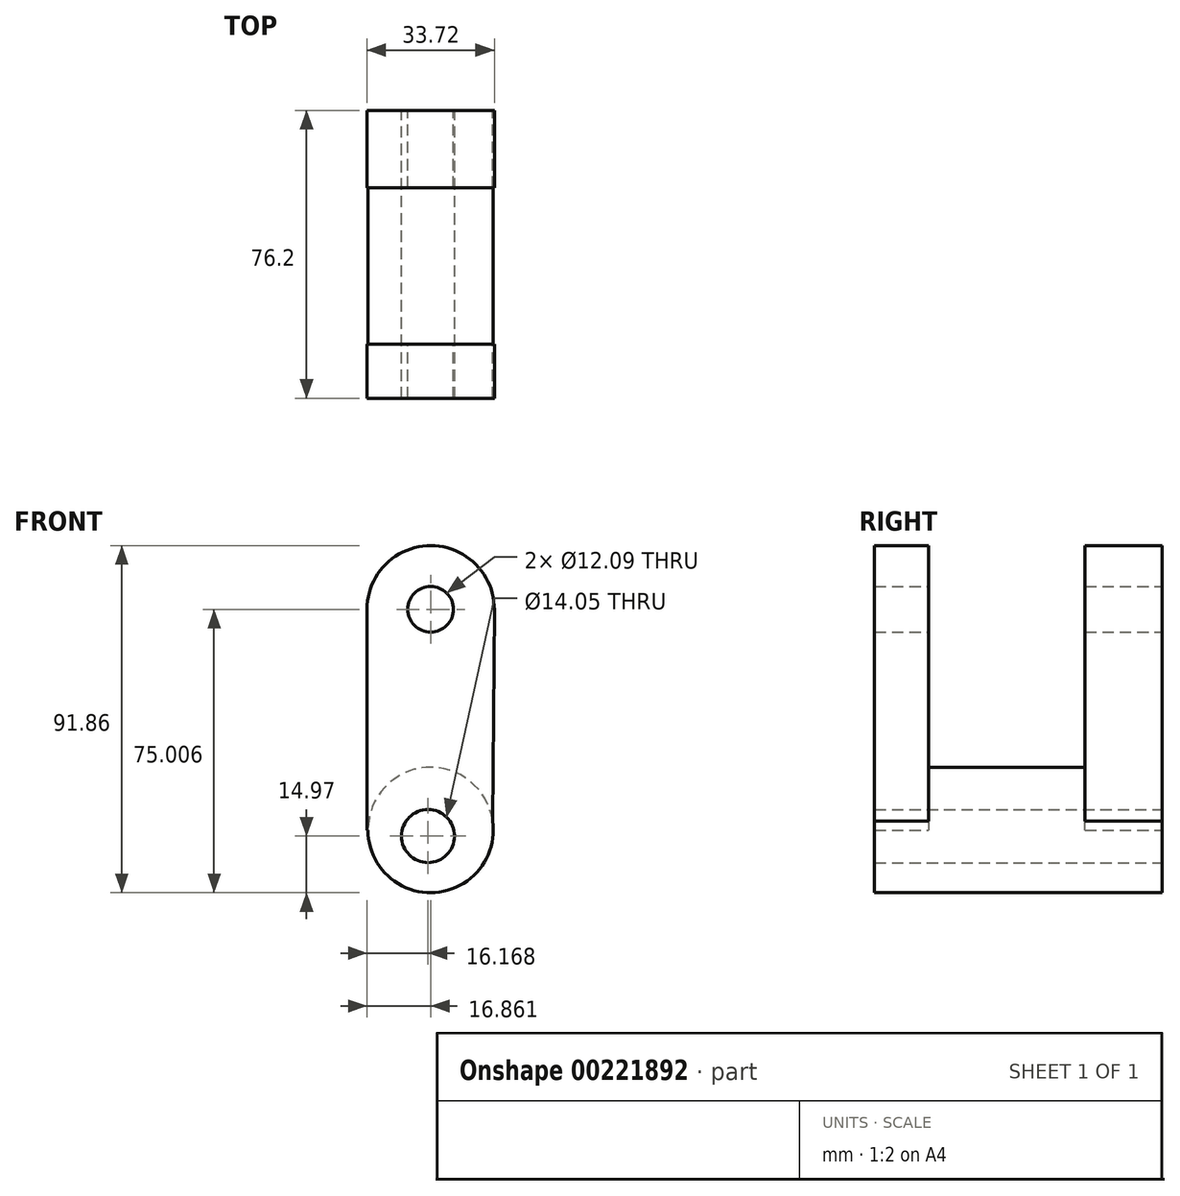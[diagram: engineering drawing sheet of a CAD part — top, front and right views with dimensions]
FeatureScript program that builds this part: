
annotation { "Feature Type Name" : "Feature", "Feature Type Description" : "" }
export const myFeature = defineFeature(function(context is Context, id is Id, definition is map)
    precondition{}
    {
        {
            var Q0;
            Q0=qCreatedBy(makeId("Front.planeOp"),FACE);
            var sketch = newSketch(context, id + "F0", { "sketchPlane" : qUnion([Q0])});
            skCircle(sketch, "E0", {"center": v(-2.3, 46.07) * mm, "radius": 16.86 * mm});
            skLineSegment(sketch, "E1", {"start": v(-19.17, 46.07) * mm, "end": v(-19.17, -12.35) * mm});
            skLineSegment(sketch, "E2", {"start": v(-19.17, -12.35) * mm, "end": v(14.09, -12.35) * mm});
            skLineSegment(sketch, "E3", {"start": v(14.09, -12.35) * mm, "end": v(14.55, 46.07) * mm});
            skSolve(sketch);
        }
        {
            var Q0;
            Q0 = qSketchRegion(id + "F0", true);
            extrude(context, id + "F1", {"entities" : qUnion([Q0]), "depth" : 38.1 * mm, "hasSecondDirection" : true, "secondDirectionOppositeDirection" : true, "secondDirectionDepth" : 38.1 * mm});
        }
        {
            var Q0;
            Q0=qCreatedBy(makeId("Right.planeOp"),FACE);
            var sketch = newSketch(context, id + "F2", { "sketchPlane" : qUnion([Q0])});
            skLineSegment(sketch, "E4", {"start": v(-23.78, 66.85) * mm, "end": v(-23.78, -12.99) * mm});
            skLineSegment(sketch, "E5", {"start": v(-23.78, -12.99) * mm, "end": v(17.64, -12.99) * mm});
            skLineSegment(sketch, "E6", {"start": v(17.64, -12.99) * mm, "end": v(17.64, 67.05) * mm});
            skLineSegment(sketch, "E7", {"start": v(17.64, 67.05) * mm, "end": v(-23.78, 66.85) * mm});
            skSolve(sketch);
        }
        {
            var Q0;
            Q0 = qSketchRegion(id + "F2", true);
            extrude(context, id + "F3", {"entities" : qUnion([Q0]), "operationType" : NewBodyOperationType.REMOVE, "endBound" : BoundingType.THROUGH_ALL, "oppositeDirection" : true, "depth" : 25.4 * mm, "hasSecondDirection" : true, "secondDirectionBound" : SecondDirectionBoundingType.THROUGH_ALL, "secondDirectionOppositeDirection" : false, "secondDirectionDepth" : 25.4 * mm});
        }
        {
            var Q0;
            Q0=qCreatedBy(makeId("Front.planeOp"),FACE);
            var sketch = newSketch(context, id + "F4", { "sketchPlane" : qUnion([Q0])});
            skCircle(sketch, "E8", {"center": v(-2.3, -12.35) * mm, "radius": 16.6 * mm});
            skSolve(sketch);
        }
        {
            var Q0;
            Q0 = qSketchRegion(id + "F4", true);
            extrude(context, id + "F5", {"entities" : qUnion([Q0]), "operationType" : NewBodyOperationType.ADD, "depth" : 38.1 * mm, "hasSecondDirection" : true, "secondDirectionOppositeDirection" : true, "secondDirectionDepth" : 38.1 * mm});
        }
        {
            var Q0;
            Q0=qCreatedBy(makeId("Front.planeOp"),FACE);
            var sketch = newSketch(context, id + "F6", { "sketchPlane" : qUnion([Q0])});
            skCircle(sketch, "E9", {"center": v(-2.3, 46.07) * mm, "radius": 6.04 * mm});
            skCircle(sketch, "E10", {"center": v(-3, -13.97) * mm, "radius": 7.02 * mm});
            skSolve(sketch);
        }
        {
            var Q0;
            Q0 = qSketchRegion(id + "F6", true);
            extrude(context, id + "F7", {"entities" : qUnion([Q0]), "operationType" : NewBodyOperationType.REMOVE, "endBound" : BoundingType.THROUGH_ALL, "depth" : 25.4 * mm, "hasSecondDirection" : true, "secondDirectionOppositeDirection" : true, "secondDirectionDepth" : 38.1 * mm});
        }
    });
